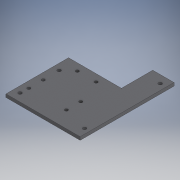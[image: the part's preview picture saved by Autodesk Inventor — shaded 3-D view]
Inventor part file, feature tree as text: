
AUTODESK INVENTOR PART (.ipt)
format: ipt  version: 2018 (Build 220112000, 112)  size: 142,848 bytes
history: native  units: mm
features: thread x4, extrude x1, sketch x1
ambient origin geometry x8: Origin, YZ Plane, XZ Plane, XY Plane, X Axis, Y Axis, Z Axis, Center Point
bodies: Solid1 (feature_tree)
feature tree (6):
  extrude  "Extrusion1"  Depth=10.0mm
  thread  "Thread1"  [1 undecoded]
  thread  "Thread2"  [1 undecoded]
  thread  "Thread3"  [1 undecoded]
  thread  "Thread4"  [1 undecoded]
  sketch  "Sketch1"  dims[d82=10.0mm d83=60.0mm d86=110.0mm d87=90.0mm d88=92.0mm d90=300.0mm d91=200.0mm d92=35.0mm d93=68.0mm d94=100.0mm d95=237.0mm d96=79.0mm d98=60.0mm d100=46.0mm d101=11.0mm d102=140.0mm d103=80.0mm d104=3.0mm d105=165.0mm d106=61.0mm d107=85.0mm d108=40.0mm d109=10.0mm d110=0.0mm d119=10.0mm d120=0.0mm d121=10.0mm d122=0.0mm d123=10.0mm d124=0.0mm d125=10.0mm d126=0.0mm d136=12.0mm d139=20.0mm]
note: 4 required parameter values undecoded (feature->parameter linkage not recoverable at this tier; creation-order binding heuristic only, values carry confidence <= 0.55)
